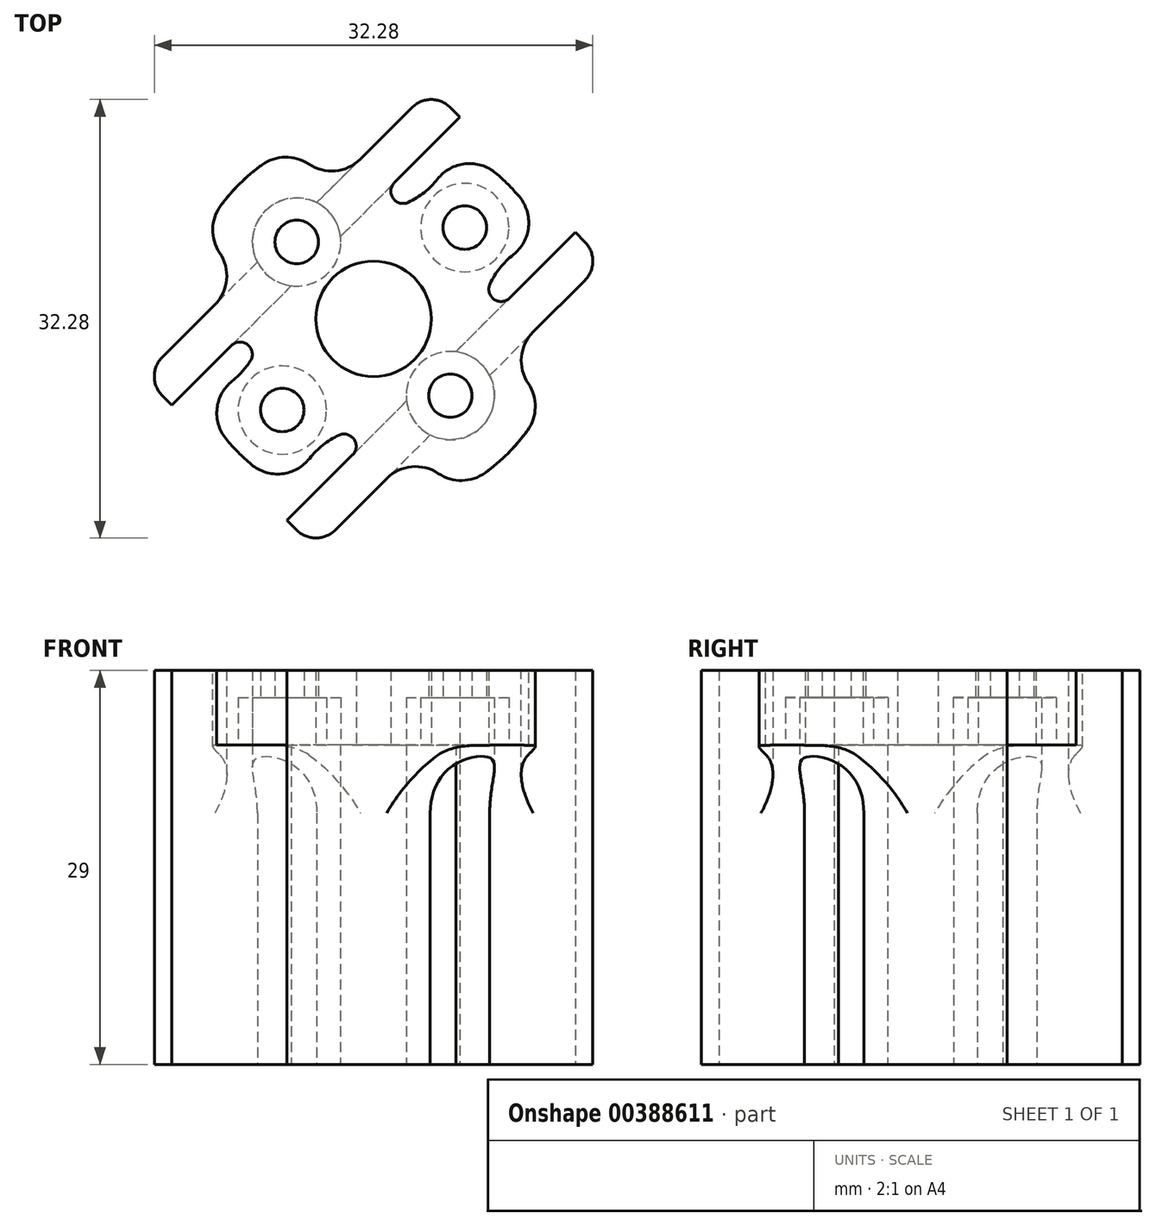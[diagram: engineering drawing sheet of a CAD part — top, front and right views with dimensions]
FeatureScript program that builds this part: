
annotation { "Feature Type Name" : "Feature", "Feature Type Description" : "" }
export const myFeature = defineFeature(function(context is Context, id is Id, definition is map)
    precondition{}
    {
        {
            assignVariable(context, id + "F0", {"name" : "wrapAroundLength", "anyValue" : 25});
        }
        {
            assignVariable(context, id + "F1", {"name" : "screwHeadDepth", "anyValue" : 3.5});
        }
        {
            var Q0;
            Q0=qCreatedBy(makeId("Top.planeOp"),FACE);
            var sketch = newSketch(context, id + "F2", { "sketchPlane" : qUnion([Q0])});
            skCircle(sketch, "E0", {"center": v(0, 0) * mm, "radius": 14 * mm});
            skLineSegment(sketch, "E1", {"start": v(0, 0) * mm, "end": v(-9.9, -9.9) * mm});
            skLineSegment(sketch, "E2", {"start": v(0, 0) * mm, "end": v(9.9, -9.9) * mm});
            skLineSegment(sketch, "E3", {"start": v(0, 0) * mm, "end": v(-9.9, 9.9) * mm});
            skLineSegment(sketch, "E4", {"start": v(0, 0) * mm, "end": v(9.9, 9.9) * mm});
            skLineSegment(sketch, "E5", {"start": v(9.9, 9.9) * mm, "end": v(10.72, 9.92) * mm});
            skCircle(sketch, "E6", {"center": v(-6.72, -6.72) * mm, "radius": 1.6 * mm});
            skCircle(sketch, "E7", {"center": v(6.72, 6.72) * mm, "radius": 1.6 * mm});
            skCircle(sketch, "E8", {"center": v(5.66, -5.66) * mm, "radius": 1.6 * mm});
            skCircle(sketch, "E9", {"center": v(-5.66, 5.66) * mm, "radius": 1.6 * mm});
            skCircle(sketch, "E10", {"center": v(0, 0) * mm, "radius": 4.25 * mm});
            skArc(sketch, "E11", {"start": v(-5.86, 12.71) * mm, "mid": v(0, 8) * mm, "end": v(5.86, 12.71) * mm});
            skArc(sketch, "E12", {"start": v(-12.78, -5.72) * mm, "mid": v(-8.13, 0.07) * mm, "end": v(-12.67, 5.95) * mm});
            skArc(sketch, "E13", {"start": v(12.71, 5.86) * mm, "mid": v(8, 0) * mm, "end": v(12.71, -5.86) * mm});
            skArc(sketch, "E14", {"start": v(5.86, -12.71) * mm, "mid": v(0, -8) * mm, "end": v(-5.86, -12.71) * mm});
            skSolve(sketch);
        }
        {
            var Q0;
            {var subQ10=sQuery(id+"F2.wireOp",EDGE,"E13");Q0=makeQuery(id+"F2.imprint","IMPRINT",FACE,{"disambiguationData":[TD([[makeQuery(id+"F2.imprint","IMPRINT",EDGE,{"derivedFrom":subQ10}),-1.0]])]});}
            var Q1;
            {var subQ7=sQuery(id+"F2.wireOp",EDGE,"E11");Q1=makeQuery(id+"F2.imprint","IMPRINT",FACE,{"disambiguationData":[TD([[makeQuery(id+"F2.imprint","IMPRINT",EDGE,{"derivedFrom":subQ7}),-1.0]])]});}
            var Q2;
            {var subQ7=sQuery(id+"F2.wireOp",EDGE,"E12");Q2=makeQuery(id+"F2.imprint","IMPRINT",FACE,{"disambiguationData":[TD([[makeQuery(id+"F2.imprint","IMPRINT",EDGE,{"derivedFrom":subQ7}),-1.0]])]});}
            var Q3;
            {var subQ10=sQuery(id+"F2.wireOp",EDGE,"E14");Q3=makeQuery(id+"F2.imprint","IMPRINT",FACE,{"disambiguationData":[TD([[makeQuery(id+"F2.imprint","IMPRINT",EDGE,{"derivedFrom":subQ10}),-1.0]])]});}
            extrude(context, id + "F3", {"entities" : qUnion([Q0, Q1, Q2, Q3]), "depth" : (getVariable(context, 'screwHeadDepth')) * mm + 2 * mm});
        }
        {
            var Q0;
            Q0=makeQuery(id+"F3.opExtrude","CAP_FACE",FACE,{"disambiguationData":[OSD([sQuery(id+"F2.wireOp",EDGE,"E0"),sQuery(id+"F2.wireOp",EDGE,"E6"),sQuery(id+"F2.wireOp",EDGE,"E7"),sQuery(id+"F2.wireOp",EDGE,"E8"),sQuery(id+"F2.wireOp",EDGE,"E9"),sQuery(id+"F2.wireOp",EDGE,"E10")])],"isStart":true});
            var sketch = newSketch(context, id + "F4", { "sketchPlane" : qUnion([Q0])});
            skCircle(sketch, "E15", {"center": v(-6.72, 6.72) * mm, "radius": 3.25 * mm});
            skCircle(sketch, "E16", {"center": v(-5.66, -5.66) * mm, "radius": 3.25 * mm});
            skCircle(sketch, "E17", {"center": v(5.66, 5.66) * mm, "radius": 3.25 * mm});
            skCircle(sketch, "E18", {"center": v(6.72, -6.72) * mm, "radius": 3.25 * mm});
            skSolve(sketch);
        }
        {
            var Q0;
            Q0 = qSketchRegion(id + "F4", true);
            extrude(context, id + "F5", {"entities" : qUnion([Q0]), "operationType" : NewBodyOperationType.REMOVE, "oppositeDirection" : true, "depth" : (getVariable(context, 'screwHeadDepth')) * mm});
        }
        {
            var Q0;
            Q0=qCreatedBy(makeId("Top.planeOp"),FACE);
            var sketch = newSketch(context, id + "F6", { "sketchPlane" : qUnion([Q0])});
            skLineSegment(sketch, "E19", {"start": v(-5.97, 5.97) * mm, "end": v(-5.97, 5.97) * mm});
            skLineSegment(sketch, "E20", {"start": v(0, 0) * mm, "end": v(-34.06, 34.06) * mm, "construction": true});
            skLineSegment(sketch, "E21", {"start": v(0, 0) * mm, "end": v(34.06, -34.06) * mm, "construction": true});
            skLineSegment(sketch, "E22", {"start": v(0, 0) * mm, "end": v(25.74, 25.74) * mm, "construction": true});
            skLineSegment(sketch, "E23", {"start": v(0, 0) * mm, "end": v(-25.74, -25.74) * mm, "construction": true});
            skLineSegment(sketch, "E24", {"start": v(-6.05, 2.43) * mm, "end": v(-14.85, -6.36) * mm});
            skLineSegment(sketch, "E25", {"start": v(-14.85, -6.36) * mm, "end": v(-16.97, -4.24) * mm});
            skLineSegment(sketch, "E26", {"start": v(-16.97, -4.24) * mm, "end": v(-8.55, 4.18) * mm});
            skCircle(sketch, "E27.0", {"center": v(-5.66, 5.66) * mm, "radius": 3.25 * mm});
            skLineSegment(sketch, "E28.MirrorCS", {"start": v(4.24, 16.97) * mm, "end": v(-4.18, 8.55) * mm});
            skLineSegment(sketch, "E29.MirrorCS", {"start": v(-2.43, 6.05) * mm, "end": v(6.36, 14.85) * mm});
            skLineSegment(sketch, "E30.MirrorCS", {"start": v(6.36, 14.85) * mm, "end": v(4.24, 16.97) * mm});
            skLineSegment(sketch, "E31.MirrorCS", {"start": v(2.43, -6.05) * mm, "end": v(-6.36, -14.85) * mm});
            skLineSegment(sketch, "E32.MirrorCS", {"start": v(-6.36, -14.85) * mm, "end": v(-4.24, -16.97) * mm});
            skLineSegment(sketch, "E33.MirrorCS", {"start": v(-4.24, -16.97) * mm, "end": v(4.18, -8.55) * mm});
            skLineSegment(sketch, "E34.MirrorCS", {"start": v(16.97, 4.24) * mm, "end": v(8.55, -4.18) * mm});
            skLineSegment(sketch, "E35.MirrorCS", {"start": v(6.05, -2.43) * mm, "end": v(14.85, 6.36) * mm});
            skLineSegment(sketch, "E36.MirrorCS", {"start": v(14.85, 6.36) * mm, "end": v(16.97, 4.24) * mm});
            skCircle(sketch, "E37.0", {"center": v(5.66, -5.66) * mm, "radius": 3.25 * mm});
            skSolve(sketch);
        }
        {
            var Q0;
            {var subQ0=sQuery(id+"F6.wireOp",EDGE,"E24");Q0=makeQuery(id+"F6.imprint","IMPRINT",FACE,{"disambiguationData":[TD([[makeQuery(id+"F6.imprint","IMPRINT",EDGE,{"derivedFrom":subQ0}),-1.0]])]});}
            var Q1;
            {var subQ0=sQuery(id+"F6.wireOp",EDGE,"E28.MirrorCS");Q1=makeQuery(id+"F6.imprint","IMPRINT",FACE,{"disambiguationData":[TD([[makeQuery(id+"F6.imprint","IMPRINT",EDGE,{"derivedFrom":subQ0}),1.0]])]});}
            var Q2;
            {var subQ0=sQuery(id+"F6.wireOp",EDGE,"E34.MirrorCS");Q2=makeQuery(id+"F6.imprint","IMPRINT",FACE,{"disambiguationData":[TD([[makeQuery(id+"F6.imprint","IMPRINT",EDGE,{"derivedFrom":subQ0}),-1.0]])]});}
            var Q3;
            {var subQ0=sQuery(id+"F6.wireOp",EDGE,"E31.MirrorCS");Q3=makeQuery(id+"F6.imprint","IMPRINT",FACE,{"disambiguationData":[TD([[makeQuery(id+"F6.imprint","IMPRINT",EDGE,{"derivedFrom":subQ0}),1.0]])]});}
            extrude(context, id + "F7", {"entities" : qUnion([Q0, Q1, Q2, Q3]), "operationType" : NewBodyOperationType.ADD, "depth" : (getVariable(context, 'screwHeadDepth')) * mm + 2 * mm, "hasSecondDirection" : true, "secondDirectionOppositeDirection" : true, "secondDirectionDepth" : (getVariable(context, 'wrapAroundLength')) * mm - (getVariable(context, 'screwHeadDepth')) * mm + 2 * mm});
        }
        {
            var Q0;
            Q0=makeQuery(id+"F7.boolean.opBoolean","INTERSECT",EDGE,{"derivedFrom":[makeQuery(id+"F3.opExtrude","SWEPT_FACE",FACE,{"disambiguationData":[OSD([sQuery(id+"F2.wireOp",EDGE,"E13")])]}),makeQuery(id+"F7.opExtrude","SWEPT_FACE",FACE,{"disambiguationData":[OSD([sQuery(id+"F6.wireOp",EDGE,"E34.MirrorCS")])]})]});
            var Q1;
            Q1=makeQuery(id+"F7.boolean.opBoolean","INTERSECT",EDGE,{"derivedFrom":[makeQuery(id+"F3.opExtrude","SWEPT_FACE",FACE,{"disambiguationData":[OSD([sQuery(id+"F2.wireOp",EDGE,"E14")])]}),makeQuery(id+"F7.opExtrude","SWEPT_FACE",FACE,{"disambiguationData":[OSD([sQuery(id+"F6.wireOp",EDGE,"E33.MirrorCS")])]})]});
            var Q2;
            Q2=makeQuery(id+"F7.boolean.opBoolean","INTERSECT",EDGE,{"derivedFrom":[makeQuery(id+"F3.opExtrude","SWEPT_FACE",FACE,{"disambiguationData":[OSD([sQuery(id+"F2.wireOp",EDGE,"E12")])]}),makeQuery(id+"F7.opExtrude","SWEPT_FACE",FACE,{"disambiguationData":[OSD([sQuery(id+"F6.wireOp",EDGE,"E26")])]})]});
            var Q3;
            Q3=makeQuery(id+"F7.boolean.opBoolean","INTERSECT",EDGE,{"derivedFrom":[makeQuery(id+"F3.opExtrude","SWEPT_FACE",FACE,{"disambiguationData":[OSD([sQuery(id+"F2.wireOp",EDGE,"E11")])]}),makeQuery(id+"F7.opExtrude","SWEPT_FACE",FACE,{"disambiguationData":[OSD([sQuery(id+"F6.wireOp",EDGE,"E28.MirrorCS")])]})]});
            fillet(context, id + "F8", {"entities" : qUnion([Q0, Q1, Q2, Q3]), "radius" : 3 * mm, "tangentPropagation" : true, "allowEdgeOverflow" : false});
        }
        {
            var Q0;
            Q0=makeQuery(id+"F7.boolean.opBoolean","INTERSECT",EDGE,{"derivedFrom":[makeQuery(id+"F3.opExtrude","SWEPT_FACE",FACE,{"disambiguationData":[OSD([sQuery(id+"F2.wireOp",EDGE,"E13")])]}),makeQuery(id+"F7.opExtrude","SWEPT_FACE",FACE,{"disambiguationData":[OSD([sQuery(id+"F6.wireOp",EDGE,"E35.MirrorCS")])]})]});
            var Q1;
            Q1=makeQuery(id+"F7.boolean.opBoolean","INTERSECT",EDGE,{"derivedFrom":[makeQuery(id+"F3.opExtrude","SWEPT_FACE",FACE,{"disambiguationData":[OSD([sQuery(id+"F2.wireOp",EDGE,"E14")])]}),makeQuery(id+"F7.opExtrude","SWEPT_FACE",FACE,{"disambiguationData":[OSD([sQuery(id+"F6.wireOp",EDGE,"E31.MirrorCS")])]})]});
            var Q2;
            Q2=makeQuery(id+"F7.boolean.opBoolean","INTERSECT",EDGE,{"derivedFrom":[makeQuery(id+"F3.opExtrude","SWEPT_FACE",FACE,{"disambiguationData":[OSD([sQuery(id+"F2.wireOp",EDGE,"E11")])]}),makeQuery(id+"F7.opExtrude","SWEPT_FACE",FACE,{"disambiguationData":[OSD([sQuery(id+"F6.wireOp",EDGE,"E29.MirrorCS")])]})]});
            var Q3;
            Q3=makeQuery(id+"F7.boolean.opBoolean","INTERSECT",EDGE,{"derivedFrom":[makeQuery(id+"F3.opExtrude","SWEPT_FACE",FACE,{"disambiguationData":[OSD([sQuery(id+"F2.wireOp",EDGE,"E12")])]}),makeQuery(id+"F7.opExtrude","SWEPT_FACE",FACE,{"disambiguationData":[OSD([sQuery(id+"F6.wireOp",EDGE,"E24")])]})]});
            fillet(context, id + "F9", {"entities" : qUnion([Q0, Q1, Q2, Q3]), "radius" : 0.9 * mm, "tangentPropagation" : true, "allowEdgeOverflow" : false});
        }
        {
            var Q0;
            {var subQ0=sQuery(id+"F2.wireOp",EDGE,"E13");var subQ1=sQuery(id+"F2.wireOp",EDGE,"E0");Q0=makeQuery(id+"F3.opExtrude","SWEPT_EDGE",EDGE,{"disambiguationData":[OSD([subQ1,subQ0]),TDD([makeQuery(id+"F2.imprint","INTERSECT",VERTEX,{"disambiguationData":[OD(0.0)],"derivedFrom":[subQ1,subQ0]})])]});}
            var Q1;
            {var subQ0=sQuery(id+"F2.wireOp",EDGE,"E11");var subQ1=sQuery(id+"F2.wireOp",EDGE,"E0");Q1=makeQuery(id+"F3.opExtrude","SWEPT_EDGE",EDGE,{"disambiguationData":[OSD([subQ1,subQ0]),TDD([makeQuery(id+"F2.imprint","INTERSECT",VERTEX,{"disambiguationData":[OD(1.0)],"derivedFrom":[subQ1,subQ0]})])]});}
            var Q2;
            {var subQ0=sQuery(id+"F2.wireOp",EDGE,"E14");var subQ1=sQuery(id+"F2.wireOp",EDGE,"E0");Q2=makeQuery(id+"F3.opExtrude","SWEPT_EDGE",EDGE,{"disambiguationData":[OSD([subQ1,subQ0]),TDD([makeQuery(id+"F2.imprint","INTERSECT",VERTEX,{"disambiguationData":[OD(1.0)],"derivedFrom":[subQ1,subQ0]})])]});}
            var Q3;
            {var subQ0=sQuery(id+"F2.wireOp",EDGE,"E12");var subQ1=sQuery(id+"F2.wireOp",EDGE,"E0");Q3=makeQuery(id+"F3.opExtrude","SWEPT_EDGE",EDGE,{"disambiguationData":[OSD([subQ1,subQ0]),TDD([makeQuery(id+"F2.imprint","INTERSECT",VERTEX,{"disambiguationData":[OD(0.0)],"derivedFrom":[subQ1,subQ0]})])]});}
            var Q4;
            {var subQ0=sQuery(id+"F2.wireOp",EDGE,"E0");var subQ1=makeQuery(id+"F2.imprint","INTERSECT",VERTEX,{"derivedFrom":[subQ0,sQuery(id+"F2.wireOp",EDGE,"E2")]});var subQ2=sQuery(id+"F2.wireOp",EDGE,"E13");Q4=makeQuery(id+"F8.opFillet","BLEND_EDGE",EDGE,{"blendedFrom":[makeQuery(id+"F7.boolean.opBoolean","INTERSECT",EDGE,{"derivedFrom":[makeQuery(id+"F3.opExtrude","SWEPT_FACE",FACE,{"disambiguationData":[OSD([subQ2])]}),makeQuery(id+"F7.opExtrude","SWEPT_FACE",FACE,{"disambiguationData":[OSD([sQuery(id+"F6.wireOp",EDGE,"E34.MirrorCS")])]})]}),makeQuery(id+"F3.opExtrude","SWEPT_FACE",FACE,{"disambiguationData":[OSD([subQ0]),TDD([makeQuery(id+"F2.imprint","IMPRINT",EDGE,{"disambiguationData":[TD([[subQ1,1.0]])],"derivedFrom":subQ0}),makeQuery(id+"F2.imprint","IMPRINT",EDGE,{"disambiguationData":[TD([[subQ1,-1.0]])],"derivedFrom":subQ0})])]})],"blendedInto":[makeQuery(id+"F3.opExtrude","SWEPT_FACE",FACE,{"disambiguationData":[OSD([subQ0]),TDD([makeQuery(id+"F2.imprint","IMPRINT",EDGE,{"disambiguationData":[TD([[subQ1,1.0]])],"derivedFrom":subQ0}),makeQuery(id+"F2.imprint","IMPRINT",EDGE,{"disambiguationData":[TD([[subQ1,-1.0]])],"derivedFrom":subQ0})])]})]});}
            var Q5;
            {var subQ0=sQuery(id+"F2.wireOp",EDGE,"E0");var subQ1=makeQuery(id+"F2.imprint","INTERSECT",VERTEX,{"derivedFrom":[subQ0,sQuery(id+"F2.wireOp",EDGE,"E2")]});var subQ2=sQuery(id+"F2.wireOp",EDGE,"E14");Q5=makeQuery(id+"F8.opFillet","BLEND_EDGE",EDGE,{"blendedFrom":[makeQuery(id+"F7.boolean.opBoolean","INTERSECT",EDGE,{"derivedFrom":[makeQuery(id+"F3.opExtrude","SWEPT_FACE",FACE,{"disambiguationData":[OSD([subQ2])]}),makeQuery(id+"F7.opExtrude","SWEPT_FACE",FACE,{"disambiguationData":[OSD([sQuery(id+"F6.wireOp",EDGE,"E33.MirrorCS")])]})]}),makeQuery(id+"F3.opExtrude","SWEPT_FACE",FACE,{"disambiguationData":[OSD([subQ0]),TDD([makeQuery(id+"F2.imprint","IMPRINT",EDGE,{"disambiguationData":[TD([[subQ1,1.0]])],"derivedFrom":subQ0}),makeQuery(id+"F2.imprint","IMPRINT",EDGE,{"disambiguationData":[TD([[subQ1,-1.0]])],"derivedFrom":subQ0})])]})],"blendedInto":[makeQuery(id+"F3.opExtrude","SWEPT_FACE",FACE,{"disambiguationData":[OSD([subQ0]),TDD([makeQuery(id+"F2.imprint","IMPRINT",EDGE,{"disambiguationData":[TD([[subQ1,1.0]])],"derivedFrom":subQ0}),makeQuery(id+"F2.imprint","IMPRINT",EDGE,{"disambiguationData":[TD([[subQ1,-1.0]])],"derivedFrom":subQ0})])]})]});}
            var Q6;
            {var subQ0=sQuery(id+"F2.wireOp",EDGE,"E0");var subQ1=makeQuery(id+"F2.imprint","INTERSECT",VERTEX,{"derivedFrom":[subQ0,sQuery(id+"F2.wireOp",EDGE,"E3")]});var subQ2=sQuery(id+"F2.wireOp",EDGE,"E12");Q6=makeQuery(id+"F8.opFillet","BLEND_EDGE",EDGE,{"blendedFrom":[makeQuery(id+"F7.boolean.opBoolean","INTERSECT",EDGE,{"derivedFrom":[makeQuery(id+"F3.opExtrude","SWEPT_FACE",FACE,{"disambiguationData":[OSD([subQ2])]}),makeQuery(id+"F7.opExtrude","SWEPT_FACE",FACE,{"disambiguationData":[OSD([sQuery(id+"F6.wireOp",EDGE,"E26")])]})]}),makeQuery(id+"F3.opExtrude","SWEPT_FACE",FACE,{"disambiguationData":[OSD([subQ0]),TDD([makeQuery(id+"F2.imprint","IMPRINT",EDGE,{"disambiguationData":[TD([[subQ1,1.0]])],"derivedFrom":subQ0}),makeQuery(id+"F2.imprint","IMPRINT",EDGE,{"disambiguationData":[TD([[subQ1,-1.0]])],"derivedFrom":subQ0})])]})],"blendedInto":[makeQuery(id+"F3.opExtrude","SWEPT_FACE",FACE,{"disambiguationData":[OSD([subQ0]),TDD([makeQuery(id+"F2.imprint","IMPRINT",EDGE,{"disambiguationData":[TD([[subQ1,1.0]])],"derivedFrom":subQ0}),makeQuery(id+"F2.imprint","IMPRINT",EDGE,{"disambiguationData":[TD([[subQ1,-1.0]])],"derivedFrom":subQ0})])]})]});}
            var Q7;
            {var subQ0=sQuery(id+"F2.wireOp",EDGE,"E0");var subQ1=makeQuery(id+"F2.imprint","INTERSECT",VERTEX,{"derivedFrom":[subQ0,sQuery(id+"F2.wireOp",EDGE,"E3")]});var subQ2=sQuery(id+"F2.wireOp",EDGE,"E11");Q7=makeQuery(id+"F8.opFillet","BLEND_EDGE",EDGE,{"blendedFrom":[makeQuery(id+"F7.boolean.opBoolean","INTERSECT",EDGE,{"derivedFrom":[makeQuery(id+"F3.opExtrude","SWEPT_FACE",FACE,{"disambiguationData":[OSD([subQ2])]}),makeQuery(id+"F7.opExtrude","SWEPT_FACE",FACE,{"disambiguationData":[OSD([sQuery(id+"F6.wireOp",EDGE,"E28.MirrorCS")])]})]}),makeQuery(id+"F3.opExtrude","SWEPT_FACE",FACE,{"disambiguationData":[OSD([subQ0]),TDD([makeQuery(id+"F2.imprint","IMPRINT",EDGE,{"disambiguationData":[TD([[subQ1,1.0]])],"derivedFrom":subQ0}),makeQuery(id+"F2.imprint","IMPRINT",EDGE,{"disambiguationData":[TD([[subQ1,-1.0]])],"derivedFrom":subQ0})])]})],"blendedInto":[makeQuery(id+"F3.opExtrude","SWEPT_FACE",FACE,{"disambiguationData":[OSD([subQ0]),TDD([makeQuery(id+"F2.imprint","IMPRINT",EDGE,{"disambiguationData":[TD([[subQ1,1.0]])],"derivedFrom":subQ0}),makeQuery(id+"F2.imprint","IMPRINT",EDGE,{"disambiguationData":[TD([[subQ1,-1.0]])],"derivedFrom":subQ0})])]})]});}
            fillet(context, id + "F10", {"entities" : qUnion([Q0, Q1, Q2, Q3, Q4, Q5, Q6, Q7]), "radius" : 3 * mm, "tangentPropagation" : true, "allowEdgeOverflow" : false});
        }
        {
            var Q0;
            Q0=makeQuery(id+"F7.boolean.opBoolean","INTERSECT",EDGE,{"derivedFrom":[makeQuery(id+"F3.opExtrude","CAP_FACE",FACE,{"disambiguationData":[OSD([sQuery(id+"F2.wireOp",EDGE,"E0"),sQuery(id+"F2.wireOp",EDGE,"E6"),sQuery(id+"F2.wireOp",EDGE,"E7"),sQuery(id+"F2.wireOp",EDGE,"E8"),sQuery(id+"F2.wireOp",EDGE,"E9"),sQuery(id+"F2.wireOp",EDGE,"E10"),sQuery(id+"F2.wireOp",EDGE,"E11"),sQuery(id+"F2.wireOp",EDGE,"E12"),sQuery(id+"F2.wireOp",EDGE,"E13"),sQuery(id+"F2.wireOp",EDGE,"E14")])],"isStart":true}),makeQuery(id+"F7.opExtrude","SWEPT_FACE",FACE,{"disambiguationData":[OSD([sQuery(id+"F6.wireOp",EDGE,"E26")])]})]});
            var Q1;
            Q1=makeQuery(id+"F7.boolean.opBoolean","INTERSECT",EDGE,{"derivedFrom":[makeQuery(id+"F3.opExtrude","CAP_FACE",FACE,{"disambiguationData":[OSD([sQuery(id+"F2.wireOp",EDGE,"E0"),sQuery(id+"F2.wireOp",EDGE,"E6"),sQuery(id+"F2.wireOp",EDGE,"E7"),sQuery(id+"F2.wireOp",EDGE,"E8"),sQuery(id+"F2.wireOp",EDGE,"E9"),sQuery(id+"F2.wireOp",EDGE,"E10"),sQuery(id+"F2.wireOp",EDGE,"E11"),sQuery(id+"F2.wireOp",EDGE,"E12"),sQuery(id+"F2.wireOp",EDGE,"E13"),sQuery(id+"F2.wireOp",EDGE,"E14")])],"isStart":true}),makeQuery(id+"F7.opExtrude","SWEPT_FACE",FACE,{"disambiguationData":[OSD([sQuery(id+"F6.wireOp",EDGE,"E33.MirrorCS")])]})]});
            fillet(context, id + "F11", {"entities" : qUnion([Q0, Q1]), "radius" : 5 * mm, "tangentPropagation" : true, "allowEdgeOverflow" : false});
        }
        {
            var Q0;
            Q0=makeQuery(id+"F7.opExtrude","SWEPT_EDGE",EDGE,{"disambiguationData":[OSD([sQuery(id+"F6.wireOp",EDGE,"E32.MirrorCS"),sQuery(id+"F6.wireOp",EDGE,"E33.MirrorCS")])]});
            var Q1;
            Q1=makeQuery(id+"F7.opExtrude","SWEPT_EDGE",EDGE,{"disambiguationData":[OSD([sQuery(id+"F6.wireOp",EDGE,"E34.MirrorCS"),sQuery(id+"F6.wireOp",EDGE,"E36.MirrorCS")])]});
            var Q2;
            Q2=makeQuery(id+"F7.opExtrude","SWEPT_EDGE",EDGE,{"disambiguationData":[OSD([sQuery(id+"F6.wireOp",EDGE,"E28.MirrorCS"),sQuery(id+"F6.wireOp",EDGE,"E30.MirrorCS")])]});
            var Q3;
            Q3=makeQuery(id+"F7.opExtrude","SWEPT_EDGE",EDGE,{"disambiguationData":[OSD([sQuery(id+"F6.wireOp",EDGE,"E25"),sQuery(id+"F6.wireOp",EDGE,"E26")])]});
            fillet(context, id + "F12", {"entities" : qUnion([Q0, Q1, Q2, Q3]), "radius" : 2 * mm, "tangentPropagation" : true, "allowEdgeOverflow" : false});
        }
    });
